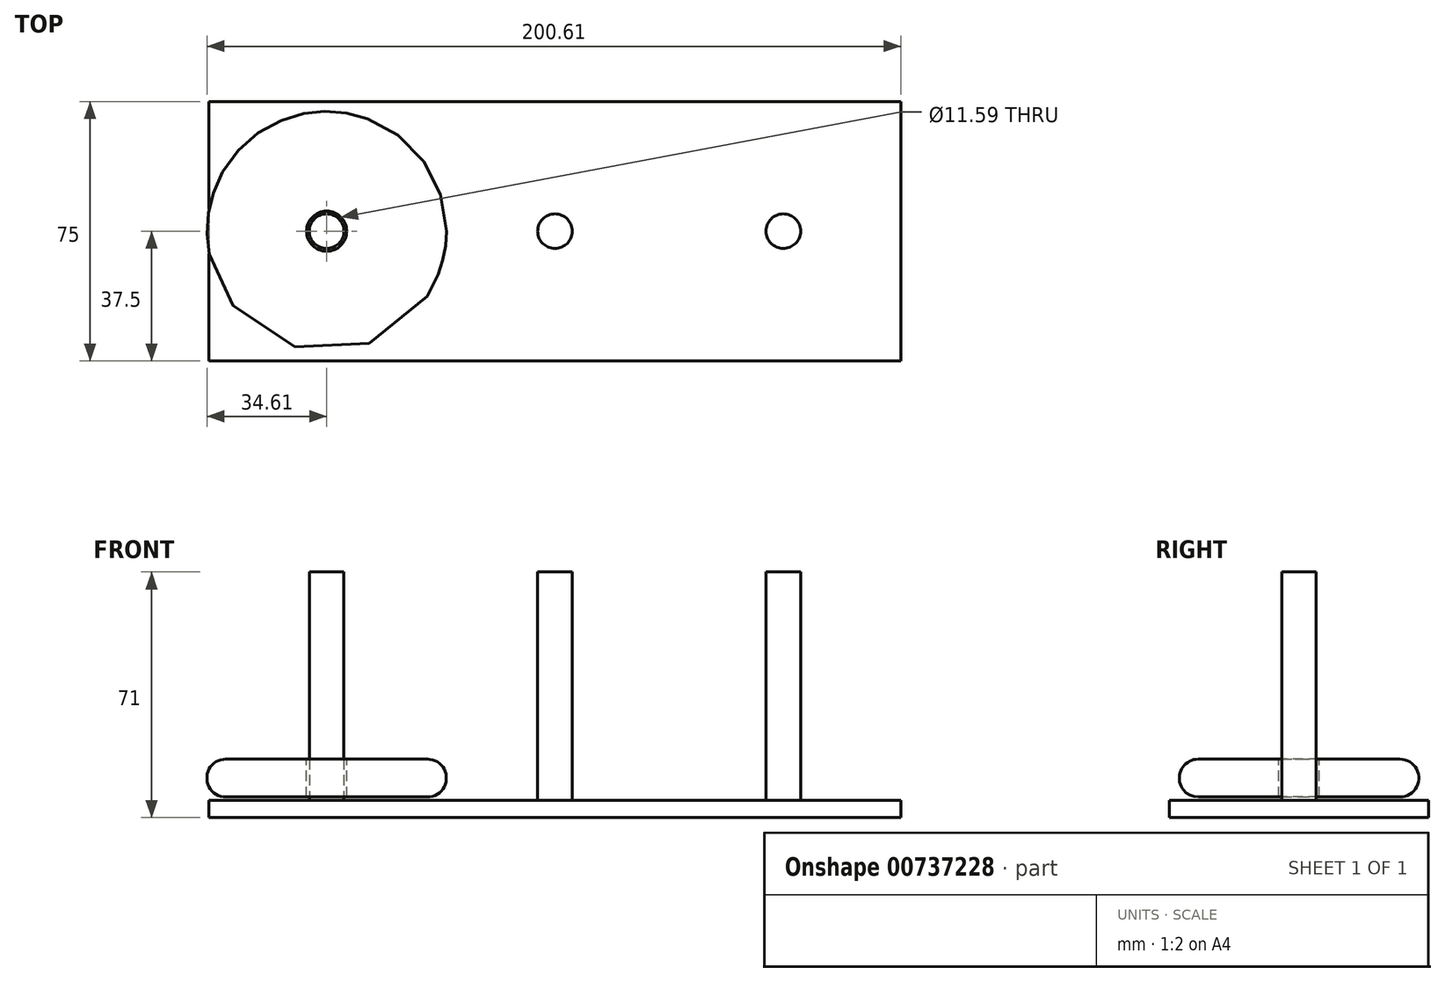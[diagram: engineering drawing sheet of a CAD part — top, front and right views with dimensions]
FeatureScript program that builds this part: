
annotation { "Feature Type Name" : "Feature", "Feature Type Description" : "" }
export const myFeature = defineFeature(function(context is Context, id is Id, definition is map)
    precondition{}
    {
        {
            var Q0;
            Q0=qCreatedBy(makeId("Top.planeOp"),FACE);
            var sketch = newSketch(context, id + "F0", { "sketchPlane" : qUnion([Q0])});
            skLineSegment(sketch, "E0.bottom", {"start": v(100, 37.5) * mm, "end": v(-100, 37.5) * mm});
            skLineSegment(sketch, "E0.top", {"start": v(100, -37.5) * mm, "end": v(-100, -37.5) * mm});
            skLineSegment(sketch, "E0.left", {"start": v(100, 37.5) * mm, "end": v(100, -37.5) * mm});
            skLineSegment(sketch, "E0.right", {"start": v(-100, 37.5) * mm, "end": v(-100, -37.5) * mm});
            skPoint(sketch, "E0.middle", {"position": v(0, 0) * mm});
            skSolve(sketch);
        }
        {
            var Q0;
            Q0=makeQuery(id+"F0.imprint","IMPRINT",FACE,{"disambiguationData":[TD([[makeQuery(id+"F0.imprint","IMPRINT",EDGE,{"derivedFrom":sQuery(id+"F0.wireOp",EDGE,"E0.bottom")}),1.0]])]});
            extrude(context, id + "F1", {"entities" : qUnion([Q0]), "depth" : 5 * mm, "offsetDistance" : 25 * mm});
        }
        {
            var Q0;
            Q0=makeQuery(id+"F1.opExtrude","CAP_FACE",FACE,{"disambiguationData":[OSD([sQuery(id+"F0.wireOp",EDGE,"E0.bottom"),sQuery(id+"F0.wireOp",EDGE,"E0.top"),sQuery(id+"F0.wireOp",EDGE,"E0.left"),sQuery(id+"F0.wireOp",EDGE,"E0.right")])],"isStart":false});
            var sketch = newSketch(context, id + "F2", { "sketchPlane" : qUnion([Q0])});
            skCircle(sketch, "E1", {"center": v(0, 0) * mm, "radius": 5 * mm});
            skCircle(sketch, "E2", {"center": v(-66, 0) * mm, "radius": 5 * mm});
            skCircle(sketch, "E3", {"center": v(66, 0) * mm, "radius": 5 * mm});
            skSolve(sketch);
        }
        {
            var Q0;
            Q0 = qSketchRegion(id + "F2", true);
            extrude(context, id + "F3", {"entities" : qUnion([Q0]), "operationType" : NewBodyOperationType.ADD, "depth" : 66 * mm, "offsetDistance" : 25 * mm});
        }
        {
            var Q0;
            Q0=makeQuery(id+"F1.opExtrude","SWEPT_FACE",FACE,{"disambiguationData":[OSD([sQuery(id+"F0.wireOp",EDGE,"E0.top")])]});
            cPlane(context, id + "F4", {"entities" : qUnion([Q0]), "cplaneType" : CPlaneType.OFFSET, "offset" : 37.5 * mm, "oppositeDirection" : true, "width" : 150 * mm, "height" : 150 * mm});
        }
        {
            var Q0;
            Q0=qCreatedBy(id+"F4.planeOp",FACE);
            var sketch = newSketch(context, id + "F5", { "sketchPlane" : qUnion([Q0])});
            skLineSegment(sketch, "E4.bottom", {"start": v(-60.2, 6.01) * mm, "end": v(-36.84, 6.01) * mm});
            skLineSegment(sketch, "E4.top", {"start": v(-60.2, 16.93) * mm, "end": v(-36.84, 16.93) * mm});
            skLineSegment(sketch, "E4.left", {"start": v(-60.2, 6.01) * mm, "end": v(-60.2, 16.93) * mm});
            skLineSegment(sketch, "E4.right", {"start": v(-36.84, 6.01) * mm, "end": v(-36.84, 16.93) * mm});
            skArc(sketch, "E5", {"start": v(-36.84, 6.01) * mm, "mid": v(-31.39, 11.47) * mm, "end": v(-36.84, 16.93) * mm});
            skSolve(sketch);
        }
        {
            var Q0;
            Q0=makeQuery(id+"F5.imprint","IMPRINT",FACE,{"disambiguationData":[TD([[makeQuery(id+"F5.imprint","IMPRINT",EDGE,{"derivedFrom":sQuery(id+"F5.wireOp",EDGE,"E4.bottom")}),1.0]])]});
            var Q1;
            Q1=makeQuery(id+"F5.imprint","IMPRINT",FACE,{"disambiguationData":[TD([[makeQuery(id+"F5.imprint","IMPRINT",EDGE,{"derivedFrom":sQuery(id+"F5.wireOp",EDGE,"E4.right")}),-1.0]])]});
            var Q2;
            Q2=sQuery(id+"F5.wireOp",EDGE,"eIg8q4Yu-TRdx-AIxk-TFNu-bt4Nj4kCyeyY");
            var Q3;
            Q3=makeQuery(id+"F3.opExtrude","SWEPT_FACE",FACE,{"disambiguationData":[OSD([sQuery(id+"F2.wireOp",EDGE,"E2")])]});
            revolve(context, id + "F6", {"surfaceOperationType" : NewSurfaceOperationType.NEW, "entities" : qUnion([Q0, Q1]), "surfaceEntities" : qUnion([Q2]), "axis" : qUnion([Q3]), "revolveType" : RevolveType.FULL});
        }
    });
